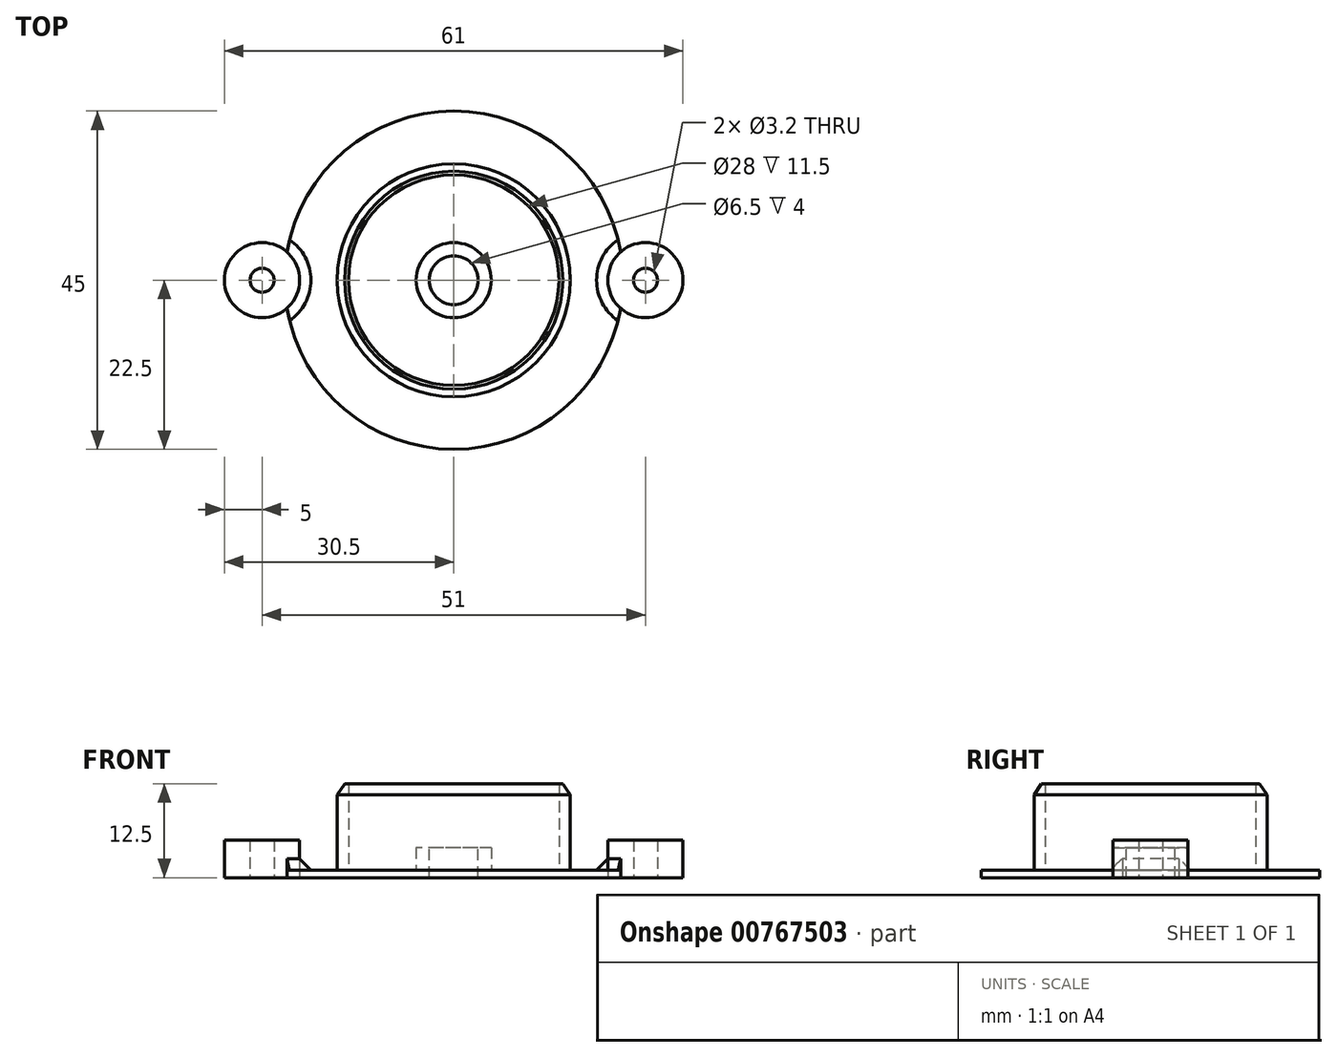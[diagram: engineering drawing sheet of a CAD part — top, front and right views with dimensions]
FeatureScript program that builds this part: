
annotation { "Feature Type Name" : "Feature", "Feature Type Description" : "" }
export const myFeature = defineFeature(function(context is Context, id is Id, definition is map)
    precondition{}
    {
        {
            var Q0;
            Q0=qCreatedBy(makeId("Top.planeOp"),FACE);
            var sketch = newSketch(context, id + "F0", { "sketchPlane" : qUnion([Q0])});
            skCircle(sketch, "E0", {"center": v(0, 0) * mm, "radius": 22.5 * mm});
            skCircle(sketch, "E1", {"center": v(25.5, 0) * mm, "radius": 5 * mm});
            skCircle(sketch, "E2", {"center": v(25.5, 0) * mm, "radius": 1.6 * mm});
            skCircle(sketch, "E3.1.0", {"center": v(-25.5, 0) * mm, "radius": 5 * mm});
            skCircle(sketch, "E3.1.1", {"center": v(-25.5, 0) * mm, "radius": 1.6 * mm});
            skSolve(sketch);
        }
        {
            var Q0;
            Q0=makeQuery(id+"F0.imprint","IMPRINT",FACE,{"disambiguationData":[TD([[makeQuery(id+"F0.imprint","IMPRINT",EDGE,{"derivedFrom":sQuery(id+"F0.wireOp",EDGE,"E3.1.1")}),-1.0]])]});
            var Q1;
            {var subQ0=sQuery(id+"F0.wireOp",EDGE,"E3.1.0");var subQ1=sQuery(id+"F0.wireOp",EDGE,"E0");var subQ2=makeQuery(id+"F0.imprint","INTERSECT",VERTEX,{"disambiguationData":[OD(0.0)],"derivedFrom":[subQ1,subQ0]});Q1=makeQuery(id+"F0.imprint","IMPRINT",FACE,{"disambiguationData":[TD([[makeQuery(id+"F0.imprint","IMPRINT",EDGE,{"disambiguationData":[TD([[subQ2,-1.0]])],"derivedFrom":subQ1}),1.0]])]});}
            var Q2;
            Q2=makeQuery(id+"F0.imprint","IMPRINT",FACE,{"disambiguationData":[TD([[makeQuery(id+"F0.imprint","IMPRINT",EDGE,{"derivedFrom":sQuery(id+"F0.wireOp",EDGE,"E2")}),-1.0]])]});
            var Q3;
            {var subQ0=sQuery(id+"F0.wireOp",EDGE,"E1");var subQ1=sQuery(id+"F0.wireOp",EDGE,"E0");var subQ2=makeQuery(id+"F0.imprint","INTERSECT",VERTEX,{"disambiguationData":[OD(0.0)],"derivedFrom":[subQ1,subQ0]});Q3=makeQuery(id+"F0.imprint","IMPRINT",FACE,{"disambiguationData":[TD([[makeQuery(id+"F0.imprint","IMPRINT",EDGE,{"disambiguationData":[TD([[subQ2,1.0]])],"derivedFrom":subQ1}),1.0]])]});}
            extrude(context, id + "F1", {"entities" : qUnion([Q0, Q1, Q2, Q3]), "depth" : 5 * mm, "offsetDistance" : 25 * mm});
        }
        {
            var Q0;
            {var subQ0=sQuery(id+"F0.wireOp",EDGE,"E3.1.0");var subQ1=sQuery(id+"F0.wireOp",EDGE,"E0");var subQ2=makeQuery(id+"F0.imprint","INTERSECT",VERTEX,{"disambiguationData":[OD(0.0)],"derivedFrom":[subQ1,subQ0]});Q0=makeQuery(id+"F0.imprint","IMPRINT",FACE,{"disambiguationData":[TD([[makeQuery(id+"F0.imprint","IMPRINT",EDGE,{"disambiguationData":[TD([[subQ2,1.0]])],"derivedFrom":subQ1}),1.0]])]});}
            extrude(context, id + "F2", {"entities" : qUnion([Q0]), "depth" : 1 * mm, "offsetDistance" : 25 * mm});
        }
        {
            var Q0;
            Q0=makeQuery(id+"F2.opExtrude","CAP_FACE",FACE,{"disambiguationData":[OSD([sQuery(id+"F0.wireOp",EDGE,"E0"),sQuery(id+"F0.wireOp",EDGE,"E1"),sQuery(id+"F0.wireOp",EDGE,"E3.1.0")])],"isStart":false});
            var sketch = newSketch(context, id + "F3", { "sketchPlane" : qUnion([Q0])});
            skCircle(sketch, "E4", {"center": v(0, 0) * mm, "radius": 14 * mm});
            skCircle(sketch, "E5", {"center": v(0, 0) * mm, "radius": 15.5 * mm});
            skSolve(sketch);
        }
        {
            var Q0;
            Q0=makeQuery(id+"F3.imprint","IMPRINT",FACE,{"disambiguationData":[TD([[makeQuery(id+"F3.imprint","IMPRINT",EDGE,{"derivedFrom":sQuery(id+"F3.wireOp",EDGE,"E4")}),-1.0]])]});
            extrude(context, id + "F4", {"entities" : qUnion([Q0]), "operationType" : NewBodyOperationType.ADD, "depth" : 11.5 * mm, "offsetDistance" : 25 * mm});
        }
        {
            var Q0;
            Q0=makeQuery(id+"F4.opExtrude","CAP_EDGE",EDGE,{"disambiguationData":[OSD([sQuery(id+"F3.wireOp",EDGE,"E5")])],"isStart":false});
            chamfer(context, id + "F5", {"entities" : qUnion([Q0]), "chamferType" : ChamferType.TWO_OFFSETS, "width1" : 1 * mm, "oppositeDirection" : false, "width2" : 1.5 * mm, "tangentPropagation" : true});
        }
        {
            var Q0;
            {var subQ0=sQuery(id+"F0.wireOp",EDGE,"E1");var subQ1=sQuery(id+"F0.wireOp",EDGE,"E3.1.0");var subQ2=sQuery(id+"F0.wireOp",EDGE,"E0");Q0=makeQuery(id+"F4.boolean.opBoolean","SPLIT",FACE,{"disambiguationData":[TD([makeQuery(id+"F2.opExtrude","SWEPT_FACE",FACE,{"disambiguationData":[OSD([subQ0])]})])],"derivedFrom":makeQuery(id+"F2.opExtrude","CAP_FACE",FACE,{"disambiguationData":[OSD([subQ2,subQ0,subQ1])],"isStart":false})});}
            var sketch = newSketch(context, id + "F6", { "sketchPlane" : qUnion([Q0])});
            skCircle(sketch, "E6", {"center": v(-25.5, 0) * mm, "radius": 6.5 * mm});
            skCircle(sketch, "E7", {"center": v(25.5, 0) * mm, "radius": 6.5 * mm});
            skSolve(sketch);
        }
        {
            var Q0;
            {var subQ1=sQuery(id+"F0.wireOp",EDGE,"E3.1.0");var subQ8=makeQuery(id+"F2.opExtrude","CAP_EDGE",EDGE,{"disambiguationData":[OSD([subQ1])],"isStart":false});Q0=makeQuery(id+"F6.imprint","IMPRINT",FACE,{"disambiguationData":[TD([[makeQuery(id+"F6.imprint","IMPRINT",EDGE,{"derivedFrom":subQ8}),-1.0]])]});}
            var Q1;
            {var subQ3=sQuery(id+"F0.wireOp",EDGE,"E1");var subQ8=makeQuery(id+"F2.opExtrude","CAP_EDGE",EDGE,{"disambiguationData":[OSD([subQ3])],"isStart":false});Q1=makeQuery(id+"F6.imprint","IMPRINT",FACE,{"disambiguationData":[TD([[makeQuery(id+"F6.imprint","IMPRINT",EDGE,{"derivedFrom":subQ8}),-1.0]])]});}
            extrude(context, id + "F7", {"entities" : qUnion([Q0, Q1]), "depth" : 1.5 * mm, "offsetDistance" : 25 * mm});
        }
        {
            var Q0;
            Q0=makeQuery(id+"F7.opExtrude","CAP_EDGE",EDGE,{"disambiguationData":[OSD([sQuery(id+"F6.wireOp",EDGE,"E6")])],"isStart":false});
            var Q1;
            Q1=makeQuery(id+"F7.opExtrude","CAP_EDGE",EDGE,{"disambiguationData":[OSD([sQuery(id+"F6.wireOp",EDGE,"E7")])],"isStart":false});
            chamfer(context, id + "F8", {"entities" : qUnion([Q0, Q1]), "width" : 1.5 * mm, "tangentPropagation" : true});
        }
        {
            var Q0;
            Q0=makeQuery(id+"F4.boolean.opBoolean","SPLIT",FACE,{"disambiguationData":[TD([makeQuery(id+"F4.opExtrude","SWEPT_FACE",FACE,{"disambiguationData":[OSD([sQuery(id+"F3.wireOp",EDGE,"E4")])]})])],"derivedFrom":makeQuery(id+"F2.opExtrude","CAP_FACE",FACE,{"disambiguationData":[OSD([sQuery(id+"F0.wireOp",EDGE,"E0"),sQuery(id+"F0.wireOp",EDGE,"E1"),sQuery(id+"F0.wireOp",EDGE,"E3.1.0")])],"isStart":false})});
            var sketch = newSketch(context, id + "F9", { "sketchPlane" : qUnion([Q0])});
            skCircle(sketch, "E8", {"center": v(0, 0) * mm, "radius": 5 * mm});
            skSolve(sketch);
        }
        {
            var Q0;
            Q0=makeQuery(id+"F9.imprint","IMPRINT",FACE,{"disambiguationData":[TD([[makeQuery(id+"F9.imprint","IMPRINT",EDGE,{"derivedFrom":sQuery(id+"F9.wireOp",EDGE,"E8")}),1.0]])]});
            extrude(context, id + "F10", {"entities" : qUnion([Q0]), "operationType" : NewBodyOperationType.ADD, "depth" : 3 * mm, "offsetDistance" : 25 * mm});
        }
        {
            var Q0;
            Q0=makeQuery(id+"F10.opExtrude","CAP_FACE",FACE,{"disambiguationData":[OSD([sQuery(id+"F9.wireOp",EDGE,"E8")])],"isStart":false});
            var sketch = newSketch(context, id + "F11", { "sketchPlane" : qUnion([Q0])});
            skCircle(sketch, "E9", {"center": v(0, 0) * mm, "radius": 3.25 * mm});
            skSolve(sketch);
        }
        {
            var Q0;
            Q0=makeQuery(id+"F11.imprint","IMPRINT",FACE,{"disambiguationData":[TD([[makeQuery(id+"F11.imprint","IMPRINT",EDGE,{"derivedFrom":sQuery(id+"F11.wireOp",EDGE,"E9")}),1.0]])]});
            extrude(context, id + "F12", {"entities" : qUnion([Q0]), "operationType" : NewBodyOperationType.REMOVE, "oppositeDirection" : true, "depth" : 5 * mm, "offsetDistance" : 25 * mm});
        }
    });
